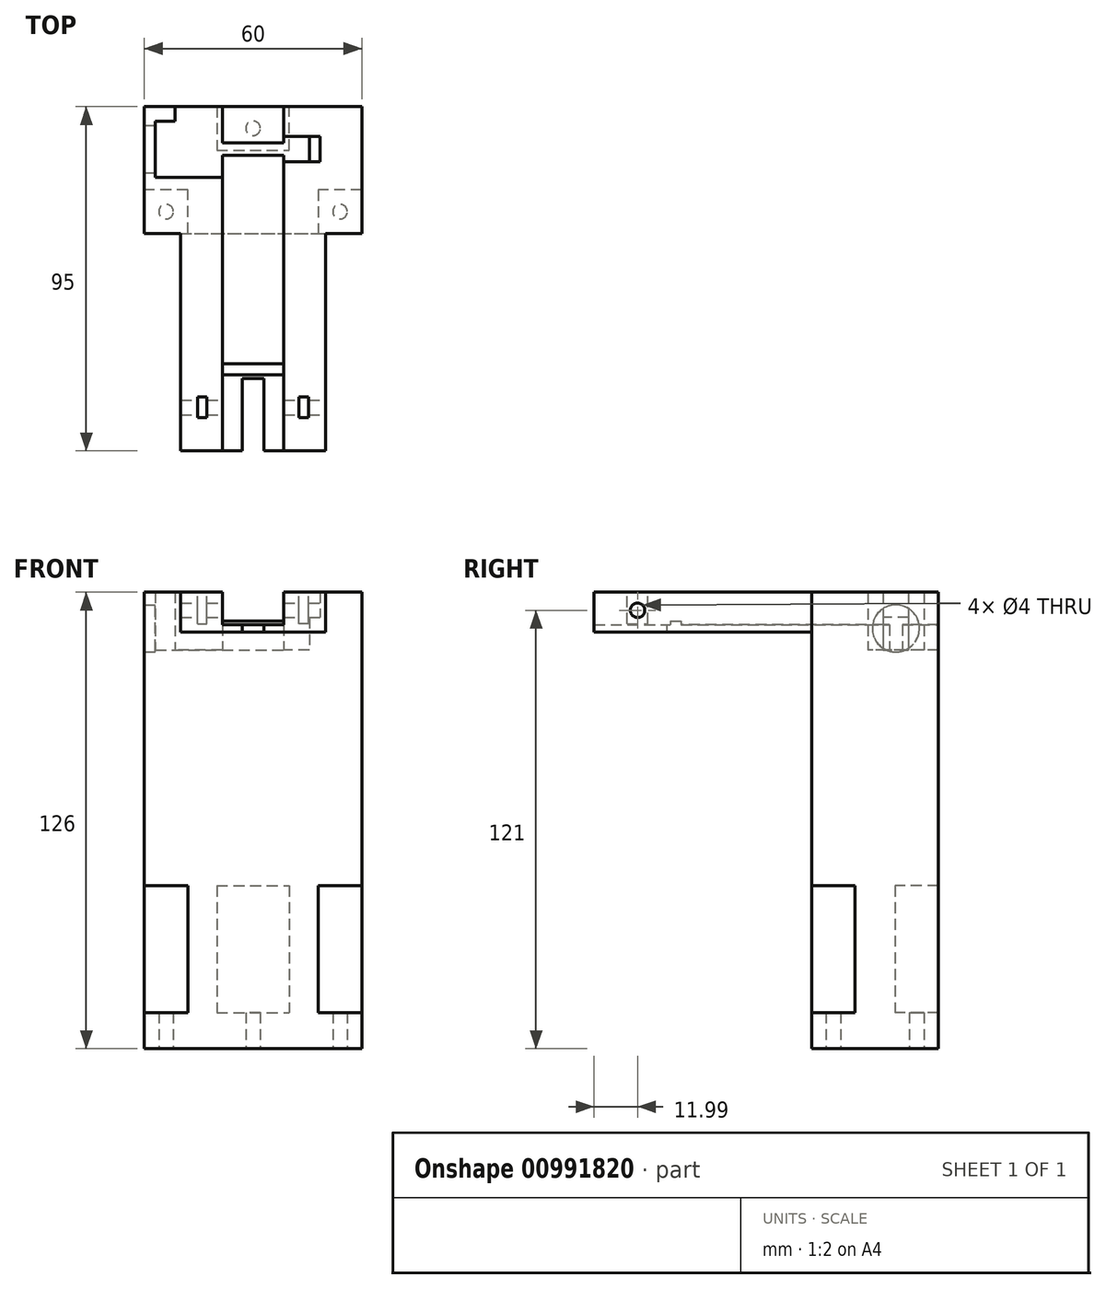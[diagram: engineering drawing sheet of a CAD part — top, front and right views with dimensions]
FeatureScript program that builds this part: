
annotation { "Feature Type Name" : "Feature", "Feature Type Description" : "" }
export const myFeature = defineFeature(function(context is Context, id is Id, definition is map)
    precondition{}
    {
        {
            var Q0;
            Q0=qCreatedBy(makeId("Top.planeOp"),FACE);
            var sketch = newSketch(context, id + "F0", { "sketchPlane" : qUnion([Q0])});
            skLineSegment(sketch, "E0.bottom", {"start": v(-30, 17.5) * mm, "end": v(30, 17.5) * mm});
            skLineSegment(sketch, "E0.top", {"start": v(-30, -17.5) * mm, "end": v(30, -17.5) * mm});
            skLineSegment(sketch, "E0.left", {"start": v(-30, 17.5) * mm, "end": v(-30, -17.5) * mm});
            skLineSegment(sketch, "E0.right", {"start": v(30, 17.5) * mm, "end": v(30, -17.5) * mm});
            skLineSegment(sketch, "E1", {"start": v(0, 17.5) * mm, "end": v(0, -17.5) * mm, "construction": true});
            skLineSegment(sketch, "E2", {"start": v(-30, 0) * mm, "end": v(30, 0) * mm, "construction": true});
            skCircle(sketch, "E3", {"center": v(0, 11.5) * mm, "radius": 2 * mm});
            skCircle(sketch, "E4", {"center": v(-24, -11.5) * mm, "radius": 2 * mm});
            skCircle(sketch, "E5.MirrorC", {"center": v(24, -11.5) * mm, "radius": 2 * mm});
            skSolve(sketch);
        }
        {
            var Q0;
            Q0 = qSketchRegion(id + "F0", true);
            extrude(context, id + "F1", {"entities" : qUnion([Q0]), "depth" : 10 * mm, "offsetDistance" : 25 * mm});
        }
        {
            var Q0;
            Q0=makeQuery(id+"F1.opExtrude","CAP_FACE",FACE,{"disambiguationData":[OSD([sQuery(id+"F0.wireOp",EDGE,"E0.bottom"),sQuery(id+"F0.wireOp",EDGE,"E0.top"),sQuery(id+"F0.wireOp",EDGE,"E0.left"),sQuery(id+"F0.wireOp",EDGE,"E0.right"),sQuery(id+"F0.wireOp",EDGE,"E3"),sQuery(id+"F0.wireOp",EDGE,"E4"),sQuery(id+"F0.wireOp",EDGE,"E5.MirrorC")])],"isStart":false});
            var sketch = newSketch(context, id + "F2", { "sketchPlane" : qUnion([Q0])});
            skLineSegment(sketch, "E6", {"start": v(-30, 17.5) * mm, "end": v(-10, 17.5) * mm});
            skLineSegment(sketch, "E7", {"start": v(-10, 17.5) * mm, "end": v(-10, 5.5) * mm});
            skLineSegment(sketch, "E8", {"start": v(-10, 5.5) * mm, "end": v(10, 5.5) * mm});
            skLineSegment(sketch, "E9", {"start": v(10, 5.5) * mm, "end": v(10, 17.5) * mm});
            skLineSegment(sketch, "E10", {"start": v(10, 17.5) * mm, "end": v(30, 17.5) * mm});
            skLineSegment(sketch, "E11", {"start": v(30, 17.5) * mm, "end": v(30, -5.5) * mm});
            skLineSegment(sketch, "E12", {"start": v(30, -5.5) * mm, "end": v(18, -5.5) * mm});
            skLineSegment(sketch, "E13", {"start": v(18, -5.5) * mm, "end": v(18, -17.5) * mm});
            skLineSegment(sketch, "E14", {"start": v(18, -17.5) * mm, "end": v(-18, -17.5) * mm});
            skLineSegment(sketch, "E15", {"start": v(-18, -17.5) * mm, "end": v(-18, -5.5) * mm});
            skLineSegment(sketch, "E16", {"start": v(-18, -5.5) * mm, "end": v(-30, -5.5) * mm});
            skLineSegment(sketch, "E17", {"start": v(-30, -5.5) * mm, "end": v(-30, 17.5) * mm});
            skSolve(sketch);
        }
        {
            var Q0;
            Q0 = qSketchRegion(id + "F2", true);
            extrude(context, id + "F3", {"entities" : qUnion([Q0]), "operationType" : NewBodyOperationType.ADD, "depth" : 35 * mm, "offsetDistance" : 25 * mm});
        }
        {
            var Q0;
            Q0=makeQuery(id+"F3.opExtrude","CAP_FACE",FACE,{"disambiguationData":[OSD([sQuery(id+"F2.wireOp",EDGE,"E6"),sQuery(id+"F2.wireOp",EDGE,"E7"),sQuery(id+"F2.wireOp",EDGE,"E8"),sQuery(id+"F2.wireOp",EDGE,"E9"),sQuery(id+"F2.wireOp",EDGE,"E10"),sQuery(id+"F2.wireOp",EDGE,"E11"),sQuery(id+"F2.wireOp",EDGE,"E12"),sQuery(id+"F2.wireOp",EDGE,"E13"),sQuery(id+"F2.wireOp",EDGE,"E14"),sQuery(id+"F2.wireOp",EDGE,"E15"),sQuery(id+"F2.wireOp",EDGE,"E16"),sQuery(id+"F2.wireOp",EDGE,"E17")])],"isStart":false});
            var sketch = newSketch(context, id + "F4", { "sketchPlane" : qUnion([Q0])});
            skLineSegment(sketch, "E18.bottom", {"start": v(-30, 17.5) * mm, "end": v(30, 17.5) * mm});
            skLineSegment(sketch, "E18.top", {"start": v(-30, -17.5) * mm, "end": v(30, -17.5) * mm});
            skLineSegment(sketch, "E18.left", {"start": v(-30, 17.5) * mm, "end": v(-30, -17.5) * mm});
            skLineSegment(sketch, "E18.right", {"start": v(30, 17.5) * mm, "end": v(30, -17.5) * mm});
            skSolve(sketch);
        }
        {
            var Q0;
            Q0 = qSketchRegion(id + "F4", true);
            extrude(context, id + "F5", {"entities" : qUnion([Q0]), "operationType" : NewBodyOperationType.ADD, "depth" : 70 * mm, "offsetDistance" : 25 * mm});
        }
        {
            var Q0;
            Q0=makeQuery(id+"F5.opExtrude","CAP_FACE",FACE,{"disambiguationData":[OSD([sQuery(id+"F4.wireOp",EDGE,"E18.bottom"),sQuery(id+"F4.wireOp",EDGE,"E18.top"),sQuery(id+"F4.wireOp",EDGE,"E18.left"),sQuery(id+"F4.wireOp",EDGE,"E18.right")])],"isStart":false});
            var sketch = newSketch(context, id + "F6", { "sketchPlane" : qUnion([Q0])});
            skLineSegment(sketch, "E19", {"start": v(-30, 17.5) * mm, "end": v(30, 17.5) * mm});
            skLineSegment(sketch, "E20", {"start": v(30, 17.5) * mm, "end": v(30, -17.5) * mm});
            skLineSegment(sketch, "E21", {"start": v(30, -17.5) * mm, "end": v(20, -17.5) * mm});
            skLineSegment(sketch, "E22", {"start": v(20, -17.5) * mm, "end": v(20, -77.5) * mm});
            skLineSegment(sketch, "E23", {"start": v(20, -77.5) * mm, "end": v(3, -77.5) * mm});
            skLineSegment(sketch, "E24", {"start": v(-20, -77.5) * mm, "end": v(-20, -17.5) * mm});
            skLineSegment(sketch, "E25", {"start": v(-20, -17.5) * mm, "end": v(-30, -17.5) * mm});
            skLineSegment(sketch, "E26", {"start": v(-30, -17.5) * mm, "end": v(-30, 17.5) * mm});
            skLineSegment(sketch, "E27", {"start": v(-3, -77.5) * mm, "end": v(-3, -57.5) * mm});
            skLineSegment(sketch, "E28", {"start": v(-3, -57.5) * mm, "end": v(3, -57.5) * mm});
            skLineSegment(sketch, "E29", {"start": v(3, -57.5) * mm, "end": v(3, -77.5) * mm});
            skLineSegment(sketch, "E30.trimOffspring", {"start": v(-3, -77.5) * mm, "end": v(-20, -77.5) * mm});
            skSolve(sketch);
        }
        {
            var Q0;
            Q0 = qSketchRegion(id + "F6", true);
            extrude(context, id + "F7", {"entities" : qUnion([Q0]), "operationType" : NewBodyOperationType.ADD, "depth" : 2 * mm, "offsetDistance" : 25 * mm});
        }
        {
            var Q0;
            Q0=makeQuery(id+"F7.opExtrude","CAP_FACE",FACE,{"disambiguationData":[OSD([sQuery(id+"F6.wireOp",EDGE,"E19"),sQuery(id+"F6.wireOp",EDGE,"E20"),sQuery(id+"F6.wireOp",EDGE,"E21"),sQuery(id+"F6.wireOp",EDGE,"E22"),sQuery(id+"F6.wireOp",EDGE,"E23"),sQuery(id+"F6.wireOp",EDGE,"E24"),sQuery(id+"F6.wireOp",EDGE,"E25"),sQuery(id+"F6.wireOp",EDGE,"E26"),sQuery(id+"F6.wireOp",EDGE,"E27"),sQuery(id+"F6.wireOp",EDGE,"E28"),sQuery(id+"F6.wireOp",EDGE,"E29"),sQuery(id+"F6.wireOp",EDGE,"E30.trimOffspring")])],"isStart":false});
            var sketch = newSketch(context, id + "F8", { "sketchPlane" : qUnion([Q0])});
            skLineSegment(sketch, "E31", {"start": v(-30, -17.5) * mm, "end": v(-30, 17.5) * mm});
            skLineSegment(sketch, "E32", {"start": v(30, 17.5) * mm, "end": v(30, -17.5) * mm});
            skLineSegment(sketch, "E33", {"start": v(30, -17.5) * mm, "end": v(20, -17.5) * mm});
            skLineSegment(sketch, "E34", {"start": v(20, -17.5) * mm, "end": v(20, -77.5) * mm});
            skLineSegment(sketch, "E35", {"start": v(20, -77.5) * mm, "end": v(8.5, -77.5) * mm});
            skLineSegment(sketch, "E36", {"start": v(8.5, -77.5) * mm, "end": v(8.5, -56.5) * mm});
            skLineSegment(sketch, "E37", {"start": v(8.5, -56.5) * mm, "end": v(-8.5, -56.5) * mm});
            skLineSegment(sketch, "E38", {"start": v(-8.5, -56.5) * mm, "end": v(-8.5, -77.5) * mm});
            skLineSegment(sketch, "E39", {"start": v(-8.5, -77.5) * mm, "end": v(-20, -77.5) * mm});
            skLineSegment(sketch, "E40", {"start": v(-20, -77.5) * mm, "end": v(-20, -17.5) * mm});
            skLineSegment(sketch, "E41", {"start": v(-20, -17.5) * mm, "end": v(-30, -17.5) * mm});
            skLineSegment(sketch, "E42", {"start": v(30, 17.5) * mm, "end": v(8.5, 17.5) * mm});
            skLineSegment(sketch, "E43", {"start": v(8.5, 17.5) * mm, "end": v(8.5, -53.5) * mm});
            skLineSegment(sketch, "E44", {"start": v(8.5, -53.5) * mm, "end": v(-8.5, -53.5) * mm});
            skLineSegment(sketch, "E45", {"start": v(-8.5, -53.5) * mm, "end": v(-8.5, 17.5) * mm});
            skLineSegment(sketch, "E46", {"start": v(-8.5, 17.5) * mm, "end": v(-30, 17.5) * mm});
            skSolve(sketch);
        }
        {
            var Q0;
            Q0 = qSketchRegion(id + "F8", true);
            extrude(context, id + "F9", {"entities" : qUnion([Q0]), "operationType" : NewBodyOperationType.ADD, "depth" : 1 * mm, "offsetDistance" : 25 * mm});
        }
        {
            var Q0;
            Q0=makeQuery(id+"F9.opExtrude","CAP_FACE",FACE,{"disambiguationData":[OSD([sQuery(id+"F8.wireOp",EDGE,"E31"),sQuery(id+"F8.wireOp",EDGE,"4YmUmNRa-hUxY-KaAa-1eh1-z22V4j9dEDoI"),sQuery(id+"F8.wireOp",EDGE,"E32"),sQuery(id+"F8.wireOp",EDGE,"E33"),sQuery(id+"F8.wireOp",EDGE,"E34"),sQuery(id+"F8.wireOp",EDGE,"E35"),sQuery(id+"F8.wireOp",EDGE,"E36"),sQuery(id+"F8.wireOp",EDGE,"E37"),sQuery(id+"F8.wireOp",EDGE,"E38"),sQuery(id+"F8.wireOp",EDGE,"E39"),sQuery(id+"F8.wireOp",EDGE,"E40"),sQuery(id+"F8.wireOp",EDGE,"E41")])],"isStart":false});
            var sketch = newSketch(context, id + "F10", { "sketchPlane" : qUnion([Q0])});
            skLineSegment(sketch, "E47", {"start": v(-8.5, -77.5) * mm, "end": v(-8.5, 17.5) * mm});
            skLineSegment(sketch, "E48", {"start": v(-8.5, 17.5) * mm, "end": v(-30, 17.5) * mm});
            skLineSegment(sketch, "E49", {"start": v(-30, 17.5) * mm, "end": v(-30, -17.5) * mm});
            skLineSegment(sketch, "E50", {"start": v(-30, -17.5) * mm, "end": v(-20, -17.5) * mm});
            skLineSegment(sketch, "E51", {"start": v(-20, -17.5) * mm, "end": v(-20, -77.5) * mm});
            skLineSegment(sketch, "E52", {"start": v(-20, -77.5) * mm, "end": v(-8.5, -77.5) * mm});
            skLineSegment(sketch, "E53.MirrorCS", {"start": v(20, -77.5) * mm, "end": v(8.5, -77.5) * mm});
            skLineSegment(sketch, "E54.MirrorCS", {"start": v(30, -17.5) * mm, "end": v(20, -17.5) * mm});
            skLineSegment(sketch, "E55.MirrorCS", {"start": v(20, -17.5) * mm, "end": v(20, -77.5) * mm});
            skLineSegment(sketch, "E56.MirrorCS", {"start": v(30, 17.5) * mm, "end": v(30, -17.5) * mm});
            skLineSegment(sketch, "E57.MirrorCS", {"start": v(8.5, 17.5) * mm, "end": v(30, 17.5) * mm});
            skLineSegment(sketch, "E58.MirrorCS", {"start": v(8.5, -77.5) * mm, "end": v(8.5, 17.5) * mm});
            skSolve(sketch);
        }
        {
            var Q0;
            Q0 = qSketchRegion(id + "F10", true);
            extrude(context, id + "F11", {"entities" : qUnion([Q0]), "operationType" : NewBodyOperationType.ADD, "depth" : 8 * mm, "offsetDistance" : 25 * mm});
        }
        {
            var Q0;
            Q0=makeQuery(id+"F11.boolean.opBoolean","MERGE",FACE,{"derivedFrom":[makeQuery(id+"F9.boolean.opBoolean","MERGE",FACE,{"derivedFrom":[makeQuery(id+"F7.opExtrude","SWEPT_FACE",FACE,{"disambiguationData":[OSD([sQuery(id+"F6.wireOp",EDGE,"E22")])]}),makeQuery(id+"F9.opExtrude","SWEPT_FACE",FACE,{"disambiguationData":[OSD([sQuery(id+"F8.wireOp",EDGE,"E34")])]})]}),makeQuery(id+"F11.opExtrude","SWEPT_FACE",FACE,{"disambiguationData":[OSD([sQuery(id+"F10.wireOp",EDGE,"E55.MirrorCS")])]})]});
            var sketch = newSketch(context, id + "F12", { "sketchPlane" : qUnion([Q0])});
            skCircle(sketch, "E59", {"center": v(-65.51, 121) * mm, "radius": 2 * mm});
            skSolve(sketch);
        }
        {
            var Q0;
            Q0 = qSketchRegion(id + "F12", true);
            extrude(context, id + "F13", {"entities" : qUnion([Q0]), "operationType" : NewBodyOperationType.REMOVE, "oppositeDirection" : true, "depth" : 45 * mm, "offsetDistance" : 25 * mm});
        }
        {
            var Q0;
            Q0=makeQuery(id+"F11.opExtrude","CAP_FACE",FACE,{"disambiguationData":[OSD([sQuery(id+"F10.wireOp",EDGE,"E53.MirrorCS"),sQuery(id+"F10.wireOp",EDGE,"E54.MirrorCS"),sQuery(id+"F10.wireOp",EDGE,"E55.MirrorCS"),sQuery(id+"F10.wireOp",EDGE,"E56.MirrorCS"),sQuery(id+"F10.wireOp",EDGE,"E57.MirrorCS"),sQuery(id+"F10.wireOp",EDGE,"E58.MirrorCS")])],"isStart":false});
            var sketch = newSketch(context, id + "F14", { "sketchPlane" : qUnion([Q0])});
            skLineSegment(sketch, "E60.bottom", {"start": v(15.3, -68.35) * mm, "end": v(12.7, -68.35) * mm});
            skLineSegment(sketch, "E60.top", {"start": v(15.3, -62.65) * mm, "end": v(12.7, -62.65) * mm});
            skLineSegment(sketch, "E60.left", {"start": v(15.3, -68.35) * mm, "end": v(15.3, -62.65) * mm});
            skLineSegment(sketch, "E60.right", {"start": v(12.7, -68.35) * mm, "end": v(12.7, -62.65) * mm});
            skLineSegment(sketch, "E61", {"start": v(15.3, -65.5) * mm, "end": v(12.7, -65.5) * mm, "construction": true});
            skLineSegment(sketch, "E62", {"start": v(14, -68.35) * mm, "end": v(14, -62.65) * mm, "construction": true});
            skLineSegment(sketch, "E63.MirrorCS", {"start": v(-15.3, -62.65) * mm, "end": v(-12.7, -62.65) * mm});
            skLineSegment(sketch, "E64.MirrorCS", {"start": v(-15.3, -68.35) * mm, "end": v(-12.7, -68.35) * mm});
            skLineSegment(sketch, "E65.MirrorCS", {"start": v(-14, -68.35) * mm, "end": v(-14, -62.65) * mm, "construction": true});
            skLineSegment(sketch, "E66.MirrorCS", {"start": v(-15.3, -68.35) * mm, "end": v(-15.3, -62.65) * mm});
            skLineSegment(sketch, "E67.MirrorCS", {"start": v(-15.3, -65.5) * mm, "end": v(-12.7, -65.5) * mm, "construction": true});
            skLineSegment(sketch, "E68.MirrorCS", {"start": v(-12.7, -68.35) * mm, "end": v(-12.7, -62.65) * mm});
            skSolve(sketch);
        }
        {
            var Q0;
            Q0 = qSketchRegion(id + "F14", true);
            extrude(context, id + "F15", {"entities" : qUnion([Q0]), "operationType" : NewBodyOperationType.REMOVE, "oppositeDirection" : true, "depth" : 8.7 * mm, "offsetDistance" : 25 * mm});
        }
        {
            var Q0;
            Q0=qCreatedBy(makeId("Top.planeOp"),FACE);
            cPlane(context, id + "F16", {"entities" : qUnion([Q0]), "cplaneType" : CPlaneType.OFFSET, "offset" : 110 * mm, "width" : 150 * mm, "height" : 150 * mm});
        }
        {
            var Q0;
            Q0=qCreatedBy(id+"F16.planeOp",FACE);
            var sketch = newSketch(context, id + "F17", { "sketchPlane" : qUnion([Q0])});
            skLineSegment(sketch, "E69.bottom", {"start": v(-27, 13.5) * mm, "end": v(-21.5, 13.5) * mm});
            skLineSegment(sketch, "E69.top", {"start": v(-27, -2) * mm, "end": v(-8.5, -2) * mm});
            skLineSegment(sketch, "E69.left", {"start": v(-27, 13.5) * mm, "end": v(-27, -2) * mm});
            skLineSegment(sketch, "E69.right", {"start": v(-8.5, 13.5) * mm, "end": v(-8.5, 7.5) * mm});
            skLineSegment(sketch, "E70", {"start": v(-8.5, 13.5) * mm, "end": v(-8.5, 17.5) * mm});
            skLineSegment(sketch, "E71", {"start": v(-8.5, 17.5) * mm, "end": v(-21.5, 17.5) * mm});
            skLineSegment(sketch, "E72", {"start": v(-21.5, 17.5) * mm, "end": v(-21.5, 13.5) * mm});
            skLineSegment(sketch, "E73", {"start": v(-8.5, 4) * mm, "end": v(8.5, 4) * mm});
            skLineSegment(sketch, "E74", {"start": v(8.5, 7.5) * mm, "end": v(-8.5, 7.5) * mm});
            skLineSegment(sketch, "E75.trimOffspring", {"start": v(-8.5, 4) * mm, "end": v(-8.5, -2) * mm});
            skLineSegment(sketch, "E76", {"start": v(8.5, 7.5) * mm, "end": v(8.5, 9.25) * mm});
            skLineSegment(sketch, "E77", {"start": v(8.5, 9.25) * mm, "end": v(15.5, 9.25) * mm});
            skLineSegment(sketch, "E78", {"start": v(15.5, 9.25) * mm, "end": v(15.5, 2.25) * mm});
            skLineSegment(sketch, "E79", {"start": v(15.5, 2.25) * mm, "end": v(8.5, 2.25) * mm});
            skLineSegment(sketch, "E80", {"start": v(8.5, 2.25) * mm, "end": v(8.5, 4) * mm});
            skSolve(sketch);
        }
        {
            var Q0;
            Q0 = qSketchRegion(id + "F17", true);
            extrude(context, id + "F18", {"entities" : qUnion([Q0]), "operationType" : NewBodyOperationType.REMOVE, "depth" : 16 * mm, "offsetDistance" : 25 * mm});
        }
        {
            var Q0;
            Q0=makeQuery(id+"F18.boolean.opBoolean","COPY",FACE,{"derivedFrom":makeQuery(id+"F18.opExtrude","SWEPT_FACE",FACE,{"disambiguationData":[OSD([sQuery(id+"F17.wireOp",EDGE,"E69.left")])]})});
            var sketch = newSketch(context, id + "F19", { "sketchPlane" : qUnion([Q0])});
            skCircle(sketch, "E81", {"center": v(5.75, 116) * mm, "radius": 6.5 * mm});
            skPoint(sketch, "E81.centerSnap0", {"position": v(5.75, 110) * mm});
            skSolve(sketch);
        }
        {
            var Q0;
            Q0 = qSketchRegion(id + "F19", true);
            extrude(context, id + "F20", {"entities" : qUnion([Q0]), "operationType" : NewBodyOperationType.REMOVE, "oppositeDirection" : true, "depth" : 5 * mm, "offsetDistance" : 25 * mm});
        }
        {
            var Q0;
            Q0=qCreatedBy(makeId("Top.planeOp"),FACE);
            cPlane(context, id + "F21", {"entities" : qUnion([Q0]), "cplaneType" : CPlaneType.OFFSET, "offset" : 114 * mm, "width" : 150 * mm, "height" : 150 * mm});
        }
        {
            var Q0;
            Q0=qCreatedBy(id+"F21.planeOp",FACE);
            var sketch = newSketch(context, id + "F22", { "sketchPlane" : qUnion([Q0])});
            skLineSegment(sketch, "E82.bottom", {"start": v(15.5, 9.25) * mm, "end": v(18.5, 9.25) * mm});
            skLineSegment(sketch, "E82.top", {"start": v(15.5, 2.25) * mm, "end": v(18.5, 2.25) * mm});
            skLineSegment(sketch, "E82.left", {"start": v(15.5, 9.25) * mm, "end": v(15.5, 2.25) * mm});
            skLineSegment(sketch, "E82.right", {"start": v(18.5, 9.25) * mm, "end": v(18.5, 2.25) * mm});
            skSolve(sketch);
        }
        {
            var Q0;
            Q0 = qSketchRegion(id + "F22", true);
            extrude(context, id + "F23", {"entities" : qUnion([Q0]), "operationType" : NewBodyOperationType.REMOVE, "depth" : 12 * mm, "offsetDistance" : 25 * mm});
        }
        {
            var Q0;
            Q0 = qSketchRegion(id + "F22", true);
            extrude(context, id + "F24", {"entities" : qUnion([Q0]), "operationType" : NewBodyOperationType.ADD, "depth" : 5 * mm, "offsetDistance" : 25 * mm});
        }
    });
